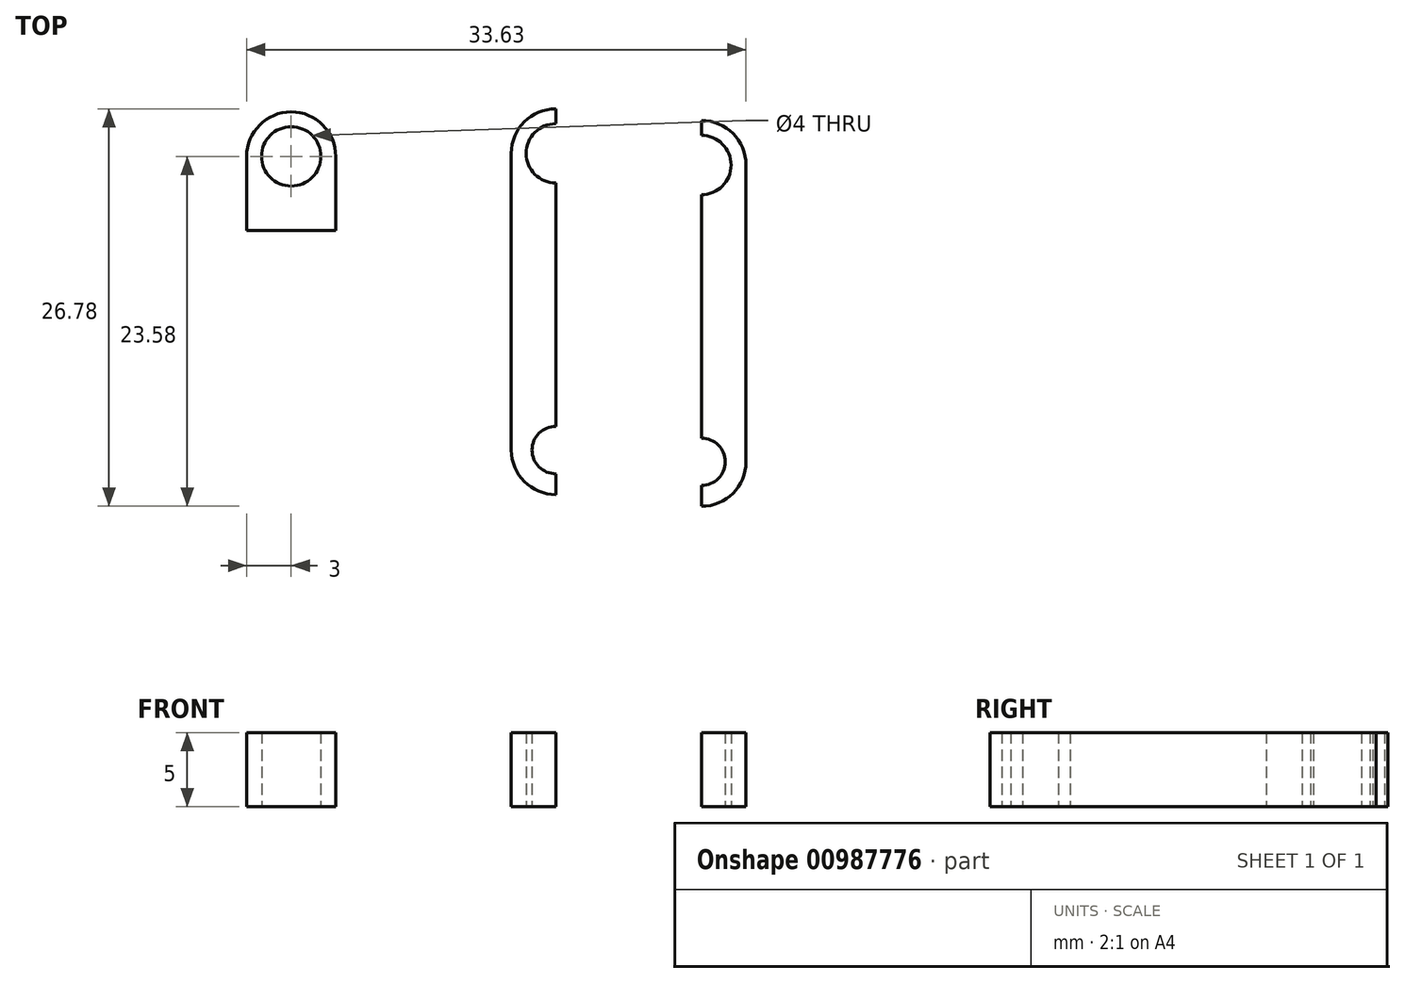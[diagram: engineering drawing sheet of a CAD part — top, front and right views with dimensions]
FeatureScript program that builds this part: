
annotation { "Feature Type Name" : "Feature", "Feature Type Description" : "" }
export const myFeature = defineFeature(function(context is Context, id is Id, definition is map)
    precondition{}
    {
        {
            var Q0;
            Q0=qCreatedBy(makeId("Top.planeOp"),FACE);
            var sketch = newSketch(context, id + "F0", { "sketchPlane" : qUnion([Q0])});
            skCircle(sketch, "E0", {"center": v(0, 0) * mm, "radius": 2 * mm});
            skArc(sketch, "E1", {"start": v(3, 0) * mm, "mid": v(0, 3) * mm, "end": v(-3, 0) * mm});
            skPoint(sketch, "E2.top.start.orphan", {"position": v(-1.5, 5) * mm});
            skPoint(sketch, "E3.orphan", {"position": v(1.5, 5) * mm});
            skLineSegment(sketch, "E4", {"start": v(-3, 0) * mm, "end": v(-3, -5) * mm});
            skLineSegment(sketch, "E5", {"start": v(3, 0) * mm, "end": v(3, -5) * mm});
            skLineSegment(sketch, "E6", {"start": v(-3, -5) * mm, "end": v(3, -5) * mm});
            skSolve(sketch);
        }
        {
            var Q0;
            Q0=makeQuery(id+"F0.imprint","IMPRINT",FACE,{"disambiguationData":[TD([[makeQuery(id+"F0.imprint","IMPRINT",EDGE,{"derivedFrom":sQuery(id+"F0.wireOp",EDGE,"E0")}),-1.0]])]});
            extrude(context, id + "F1", {"entities" : qUnion([Q0]), "depth" : 5 * mm, "offsetDistance" : 25 * mm});
        }
        {
            var Q0;
            Q0=qCreatedBy(makeId("Top.planeOp"),FACE);
            var sketch = newSketch(context, id + "F2", { "sketchPlane" : qUnion([Q0])});
            skArc(sketch, "E7", {"start": v(17.82, 2.2) * mm, "mid": v(15.82, 0.2) * mm, "end": v(17.82, -1.8) * mm});
            skArc(sketch, "E8", {"start": v(17.82, 3.2) * mm, "mid": v(15.7, 2.33) * mm, "end": v(14.82, 0.2) * mm});
            skPoint(sketch, "E9.top.start.orphan", {"position": v(16.32, 3.67) * mm});
            skPoint(sketch, "E10.orphan", {"position": v(19.32, 3.67) * mm});
            skArc(sketch, "E11", {"start": v(17.82, -18.2) * mm, "mid": v(16.22, -19.8) * mm, "end": v(17.82, -21.4) * mm});
            skArc(sketch, "E12", {"start": v(14.82, -19.8) * mm, "mid": v(15.7, -21.92) * mm, "end": v(17.82, -22.8) * mm});
            skLineSegment(sketch, "E13", {"start": v(14.82, 0.2) * mm, "end": v(14.82, -19.8) * mm});
            skCircle(sketch, "E14", {"center": v(45.05, -1.75) * mm, "radius": 2 * mm});
            skArc(sketch, "E15", {"start": v(48.05, -1.75) * mm, "mid": v(45.05, 1.25) * mm, "end": v(42.05, -1.75) * mm});
            skPoint(sketch, "E16.top.start.orphan", {"position": v(43.55, 1.72) * mm});
            skPoint(sketch, "E17.orphan", {"position": v(46.55, 1.72) * mm});
            skCircle(sketch, "E18", {"center": v(45.05, -21.75) * mm, "radius": 1.6 * mm});
            skArc(sketch, "E19", {"start": v(42.05, -21.75) * mm, "mid": v(45.05, -24.75) * mm, "end": v(48.05, -21.75) * mm});
            skLineSegment(sketch, "E20", {"start": v(42.05, -1.75) * mm, "end": v(42.05, -21.75) * mm});
            skLineSegment(sketch, "E21", {"start": v(48.05, -1.75) * mm, "end": v(48.05, -21.75) * mm});
            skLineSegment(sketch, "E22", {"start": v(17.82, 3.2) * mm, "end": v(17.82, 2.2) * mm});
            skLineSegment(sketch, "E23.trimOffspring", {"start": v(17.82, -1.8) * mm, "end": v(17.82, -18.2) * mm});
            skLineSegment(sketch, "E24.trimOffspring", {"start": v(17.82, -21.4) * mm, "end": v(17.82, -22.8) * mm});
            skPoint(sketch, "E25.orphan", {"position": v(20.82, -19.8) * mm});
            skSolve(sketch);
        }
        {
            var Q0;
            Q0=makeQuery(id+"F2.imprint","IMPRINT",FACE,{"disambiguationData":[TD([[makeQuery(id+"F2.imprint","IMPRINT",EDGE,{"derivedFrom":sQuery(id+"F2.wireOp",EDGE,"E7")}),-1.0]])]});
            extrude(context, id + "F3", {"entities" : qUnion([Q0]), "depth" : 5 * mm, "offsetDistance" : 25 * mm});
        }
        {
            var Q0;
            Q0=qCreatedBy(makeId("Top.planeOp"),FACE);
            var sketch = newSketch(context, id + "F4", { "sketchPlane" : qUnion([Q0])});
            skArc(sketch, "E26", {"start": v(27.63, -2.58) * mm, "mid": v(29.63, -0.58) * mm, "end": v(27.63, 1.42) * mm});
            skArc(sketch, "E27", {"start": v(30.63, -0.58) * mm, "mid": v(29.75, 1.54) * mm, "end": v(27.63, 2.42) * mm});
            skPoint(sketch, "E28.top.start.orphan", {"position": v(26.13, 2.88) * mm});
            skPoint(sketch, "E29.orphan", {"position": v(29.13, 2.88) * mm});
            skArc(sketch, "E30", {"start": v(27.63, -22.18) * mm, "mid": v(29.23, -20.58) * mm, "end": v(27.63, -18.98) * mm});
            skArc(sketch, "E31", {"start": v(27.63, -23.58) * mm, "mid": v(29.75, -22.7) * mm, "end": v(30.63, -20.58) * mm});
            skLineSegment(sketch, "E32", {"start": v(30.63, -0.58) * mm, "end": v(30.63, -20.58) * mm});
            skLineSegment(sketch, "E33", {"start": v(27.63, 2.42) * mm, "end": v(27.63, 1.42) * mm});
            skPoint(sketch, "E34.orphan", {"position": v(24.63, -20.58) * mm});
            skLineSegment(sketch, "E35.trimOffspring", {"start": v(27.63, -22.18) * mm, "end": v(27.63, -23.58) * mm});
            skLineSegment(sketch, "E36.trimOffspring", {"start": v(27.63, -2.58) * mm, "end": v(27.63, -18.98) * mm});
            skSolve(sketch);
        }
        {
            var Q0;
            Q0=makeQuery(id+"F4.imprint","IMPRINT",FACE,{"disambiguationData":[TD([[makeQuery(id+"F4.imprint","IMPRINT",EDGE,{"derivedFrom":sQuery(id+"F4.wireOp",EDGE,"E26")}),-1.0]])]});
            extrude(context, id + "F5", {"entities" : qUnion([Q0]), "depth" : 5 * mm, "offsetDistance" : 25 * mm});
        }
    });
